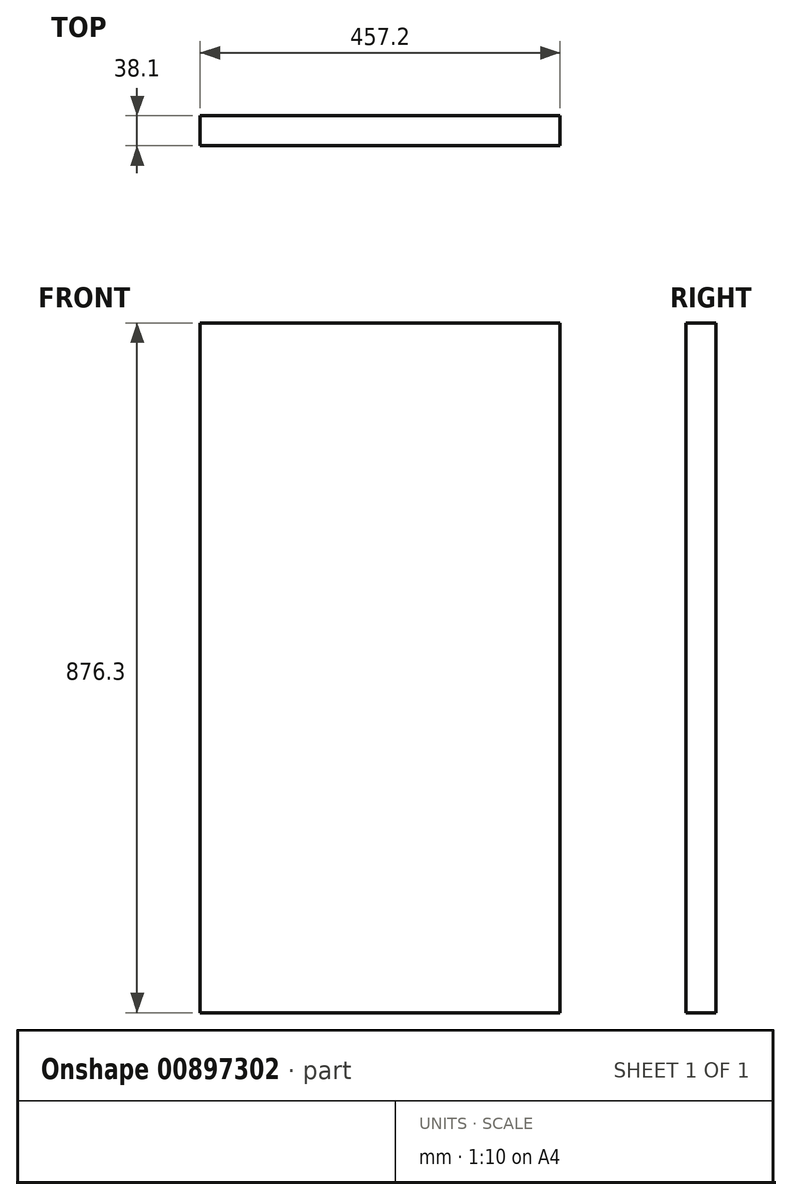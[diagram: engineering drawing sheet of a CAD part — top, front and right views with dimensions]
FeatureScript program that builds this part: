
annotation { "Feature Type Name" : "Feature", "Feature Type Description" : "" }
export const myFeature = defineFeature(function(context is Context, id is Id, definition is map)
    precondition{}
    {
        {
            var Q0;
            Q0=qCreatedBy(makeId("Front.planeOp"),FACE);
            var sketch = newSketch(context, id + "F0", { "sketchPlane" : qUnion([Q0])});
            skLineSegment(sketch, "E0.bottom", {"start": v(-417.43, 818.49) * mm, "end": v(39.77, 818.49) * mm});
            skLineSegment(sketch, "E0.top", {"start": v(-417.43, -57.81) * mm, "end": v(39.77, -57.81) * mm});
            skLineSegment(sketch, "E0.left", {"start": v(-417.43, 818.49) * mm, "end": v(-417.43, -57.81) * mm});
            skLineSegment(sketch, "E0.right", {"start": v(39.77, 818.49) * mm, "end": v(39.77, -57.81) * mm});
            skSolve(sketch);
        }
        {
            var Q0;
            Q0=makeQuery(id+"F0.imprint","IMPRINT",FACE,{"disambiguationData":[TD([[makeQuery(id+"F0.imprint","IMPRINT",EDGE,{"derivedFrom":sQuery(id+"F0.wireOp",EDGE,"E0.bottom")}),-1.0]])]});
            extrude(context, id + "F1", {"entities" : qUnion([Q0]), "depth" : 38.1 * mm, "offsetDistance" : 25.4 * mm});
        }
    });
